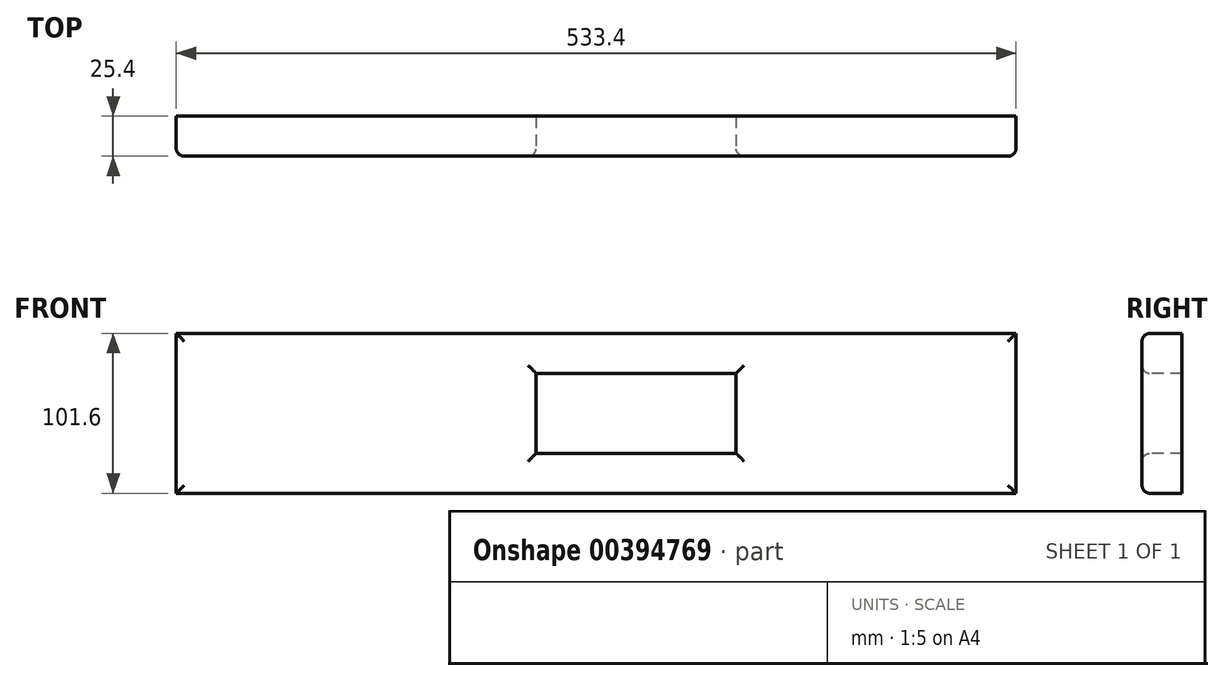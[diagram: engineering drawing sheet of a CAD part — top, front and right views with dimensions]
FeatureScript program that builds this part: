
annotation { "Feature Type Name" : "Feature", "Feature Type Description" : "" }
export const myFeature = defineFeature(function(context is Context, id is Id, definition is map)
    precondition{}
    {
        {
            var Q0;
            Q0=qCreatedBy(makeId("Front.planeOp"),FACE);
            var sketch = newSketch(context, id + "F0", { "sketchPlane" : qUnion([Q0])});
            skLineSegment(sketch, "E0.bottom", {"start": v(0, 0) * mm, "end": v(-533.4, 0) * mm});
            skLineSegment(sketch, "E0.top", {"start": v(0, -101.6) * mm, "end": v(-533.4, -101.6) * mm});
            skLineSegment(sketch, "E0.left", {"start": v(0, 0) * mm, "end": v(0, -101.6) * mm});
            skLineSegment(sketch, "E0.right", {"start": v(-533.4, 0) * mm, "end": v(-533.4, -101.6) * mm});
            skSolve(sketch);
        }
        {
            var Q0;
            Q0=makeQuery(id+"F0.imprint","IMPRINT",FACE,{"disambiguationData":[TD([[makeQuery(id+"F0.imprint","IMPRINT",EDGE,{"derivedFrom":sQuery(id+"F0.wireOp",EDGE,"E0.bottom")}),1.0]])]});
            extrude(context, id + "F1", {"entities" : qUnion([Q0]), "depth" : 25.4 * mm});
        }
        {
            var Q0;
            Q0=makeQuery(id+"F1.opExtrude","CAP_FACE",FACE,{"disambiguationData":[OSD([sQuery(id+"F0.wireOp",EDGE,"E0.bottom"),sQuery(id+"F0.wireOp",EDGE,"E0.top"),sQuery(id+"F0.wireOp",EDGE,"E0.left"),sQuery(id+"F0.wireOp",EDGE,"E0.right")])],"isStart":false});
            var sketch = newSketch(context, id + "F2", { "sketchPlane" : qUnion([Q0])});
            skLineSegment(sketch, "E1.bottom", {"start": v(-304.8, -76.2) * mm, "end": v(-177.8, -76.2) * mm});
            skLineSegment(sketch, "E1.top", {"start": v(-304.8, -25.4) * mm, "end": v(-177.8, -25.4) * mm});
            skLineSegment(sketch, "E1.left", {"start": v(-304.8, -76.2) * mm, "end": v(-304.8, -25.4) * mm});
            skLineSegment(sketch, "E1.right", {"start": v(-177.8, -76.2) * mm, "end": v(-177.8, -25.4) * mm});
            skSolve(sketch);
        }
        {
            var Q0;
            Q0=makeQuery(id+"F2.imprint","IMPRINT",FACE,{"disambiguationData":[TD([[makeQuery(id+"F2.imprint","IMPRINT",EDGE,{"derivedFrom":sQuery(id+"F2.wireOp",EDGE,"E1.bottom")}),1.0]])]});
            extrude(context, id + "F3", {"entities" : qUnion([Q0]), "operationType" : NewBodyOperationType.REMOVE, "oppositeDirection" : true, "depth" : 50.8 * mm});
        }
        {
            var Q0;
            Q0=makeQuery(id+"F1.opExtrude","CAP_FACE",FACE,{"disambiguationData":[OSD([sQuery(id+"F0.wireOp",EDGE,"E0.bottom"),sQuery(id+"F0.wireOp",EDGE,"E0.top"),sQuery(id+"F0.wireOp",EDGE,"E0.left"),sQuery(id+"F0.wireOp",EDGE,"E0.right")])],"isStart":false});
            fillet(context, id + "F4", {"entities" : qUnion([Q0]), "radius" : 5.08 * mm, "tangentPropagation" : true, "allowEdgeOverflow" : false});
        }
    });
